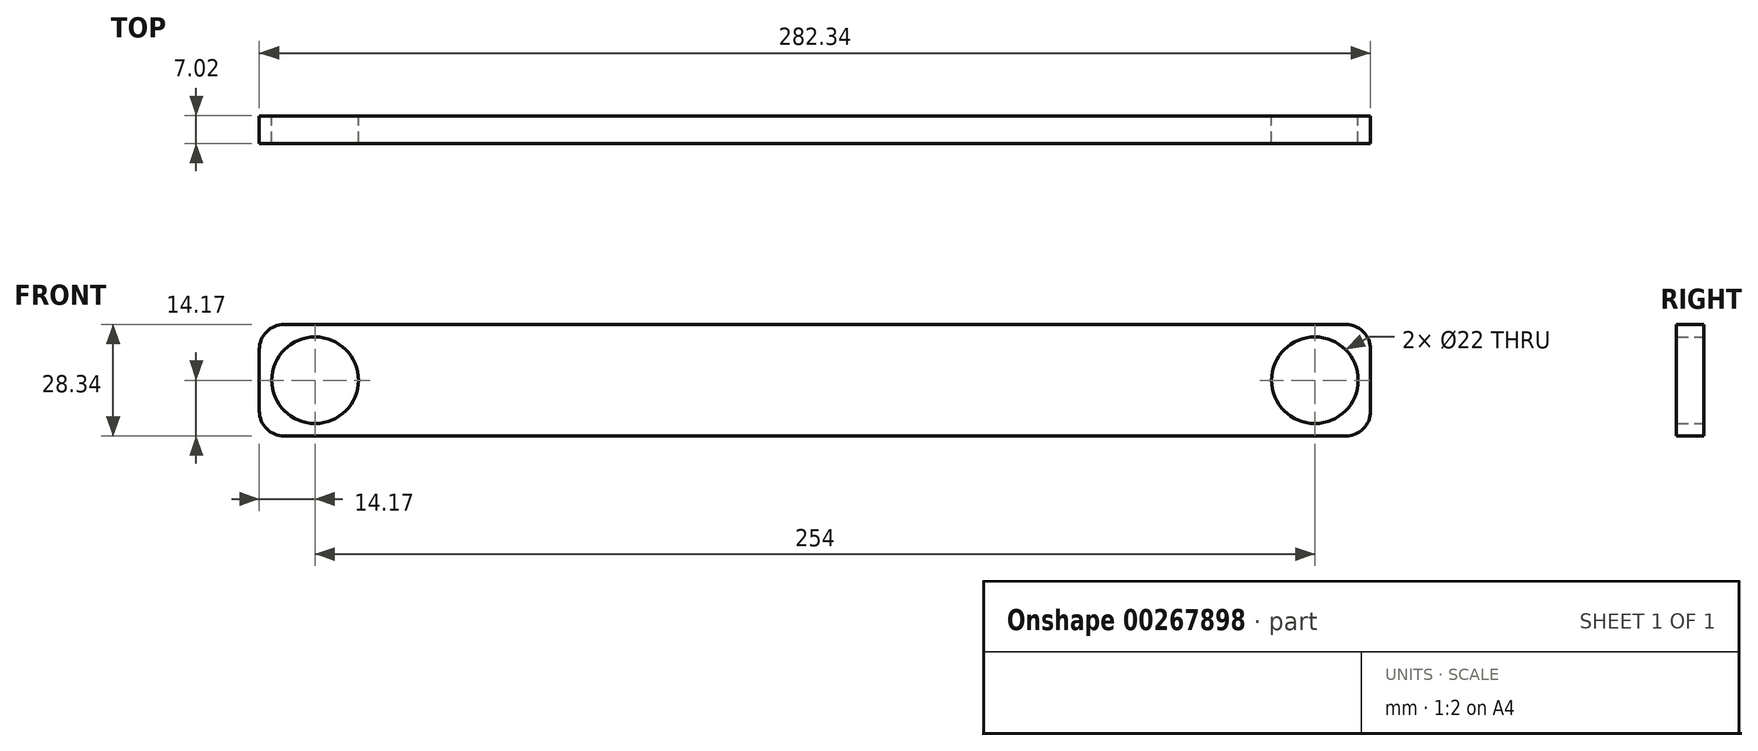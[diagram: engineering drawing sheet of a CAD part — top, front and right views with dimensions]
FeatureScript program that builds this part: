
annotation { "Feature Type Name" : "Feature", "Feature Type Description" : "" }
export const myFeature = defineFeature(function(context is Context, id is Id, definition is map)
    precondition{}
    {
        {
            var Q0;
            Q0=qCreatedBy(makeId("Front.planeOp"),FACE);
            var sketch = newSketch(context, id + "F0", { "sketchPlane" : qUnion([Q0])});
            skLineSegment(sketch, "E0.bottom", {"start": v(141.17, 14.17) * mm, "end": v(-141.17, 14.17) * mm});
            skLineSegment(sketch, "E0.top", {"start": v(141.17, -14.17) * mm, "end": v(-141.17, -14.17) * mm});
            skLineSegment(sketch, "E0.left", {"start": v(141.17, 14.17) * mm, "end": v(141.17, -14.17) * mm});
            skLineSegment(sketch, "E0.right", {"start": v(-141.17, 14.17) * mm, "end": v(-141.17, -14.17) * mm});
            skPoint(sketch, "E0.middle", {"position": v(0, 0) * mm});
            skCircle(sketch, "E1", {"center": v(-127, 0) * mm, "radius": 11 * mm});
            skCircle(sketch, "E2.MirrorC", {"center": v(127, 0) * mm, "radius": 11 * mm});
            skSolve(sketch);
        }
        {
            var Q0;
            Q0=makeQuery(id+"F0.imprint","IMPRINT",FACE,{"disambiguationData":[TD([[makeQuery(id+"F0.imprint","IMPRINT",EDGE,{"derivedFrom":sQuery(id+"F0.wireOp",EDGE,"E0.bottom")}),1.0]])]});
            extrude(context, id + "F1", {"entities" : qUnion([Q0]), "endBound" : BoundingType.SYMMETRIC, "depth" : 7 * mm});
        }
        {
            var Q0;
            Q0=makeQuery(id+"F1.opExtrude","SWEPT_EDGE",EDGE,{"disambiguationData":[OSD([sQuery(id+"F0.wireOp",EDGE,"E0.bottom"),sQuery(id+"F0.wireOp",EDGE,"E0.right")])]});
            var Q1;
            Q1=makeQuery(id+"F1.opExtrude","SWEPT_EDGE",EDGE,{"disambiguationData":[OSD([sQuery(id+"F0.wireOp",EDGE,"E0.top"),sQuery(id+"F0.wireOp",EDGE,"E0.right")])]});
            var Q2;
            Q2=makeQuery(id+"F1.opExtrude","SWEPT_EDGE",EDGE,{"disambiguationData":[OSD([sQuery(id+"F0.wireOp",EDGE,"E0.bottom"),sQuery(id+"F0.wireOp",EDGE,"E0.left")])]});
            var Q3;
            Q3=makeQuery(id+"F1.opExtrude","SWEPT_EDGE",EDGE,{"disambiguationData":[OSD([sQuery(id+"F0.wireOp",EDGE,"E0.top"),sQuery(id+"F0.wireOp",EDGE,"E0.left")])]});
            fillet(context, id + "F2", {"entities" : qUnion([Q0, Q1, Q2, Q3]), "radius" : 6.35 * mm, "tangentPropagation" : true, "allowEdgeOverflow" : false});
        }
    });
